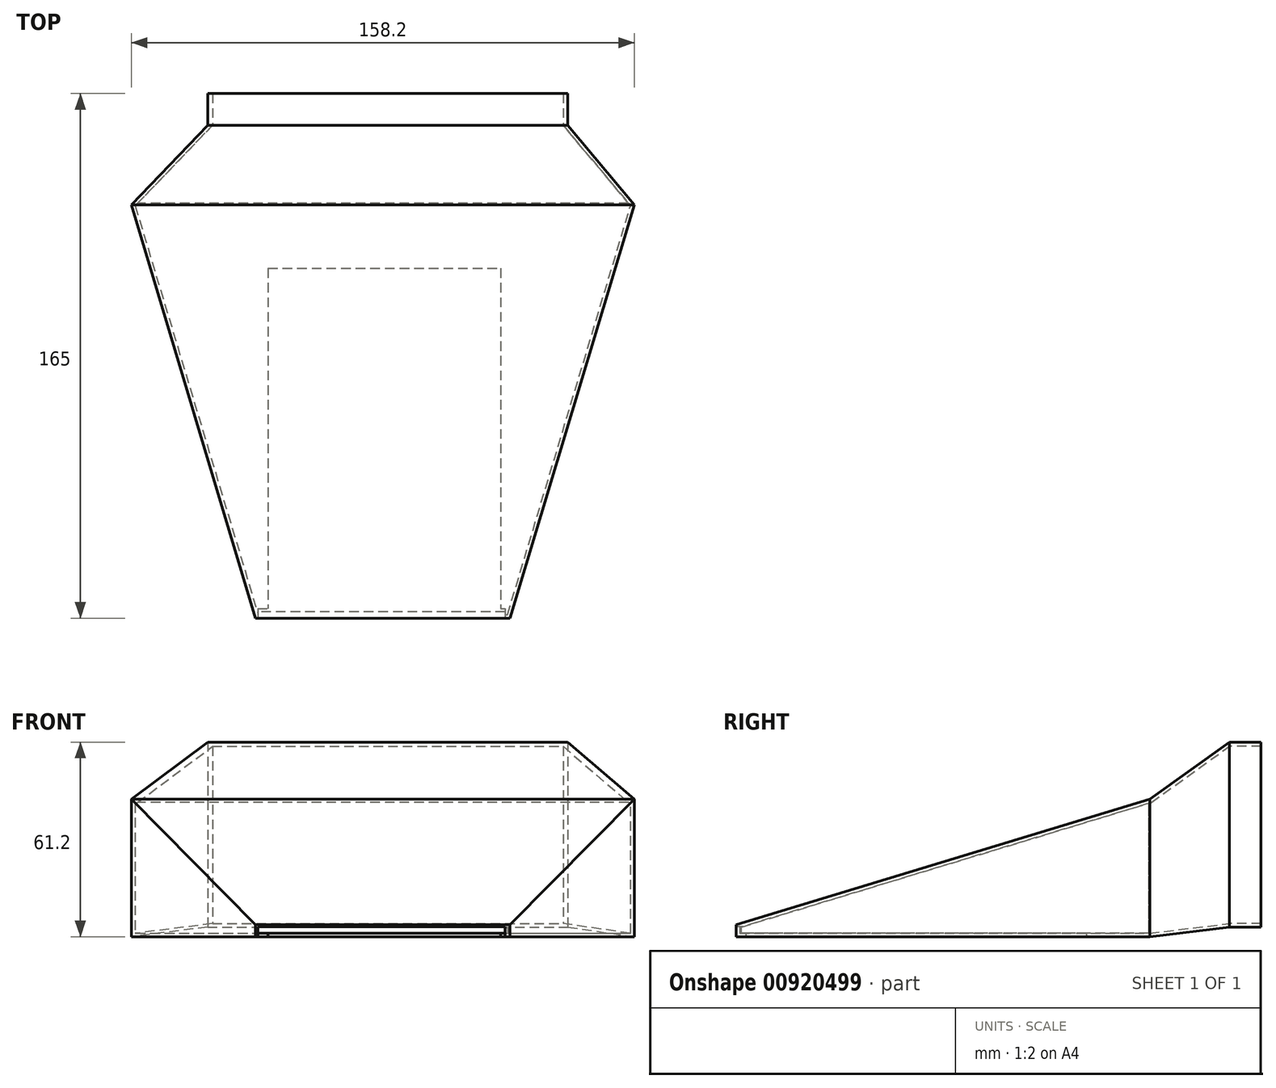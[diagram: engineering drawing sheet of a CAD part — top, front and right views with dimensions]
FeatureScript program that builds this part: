
annotation { "Feature Type Name" : "Feature", "Feature Type Description" : "" }
export const myFeature = defineFeature(function(context is Context, id is Id, definition is map)
    precondition{}
    {
        {
            var Q0;
            Q0=qCreatedBy(makeId("Front.planeOp"),FACE);
            var sketch = newSketch(context, id + "F0", { "sketchPlane" : qUnion([Q0])});
            skLineSegment(sketch, "E0.bottom", {"start": v(-55.06, 61.2) * mm, "end": v(58.14, 61.2) * mm});
            skLineSegment(sketch, "E0.top", {"start": v(-55.06, 3) * mm, "end": v(58.14, 3) * mm});
            skLineSegment(sketch, "E0.left", {"start": v(-55.06, 61.2) * mm, "end": v(-55.06, 3) * mm});
            skLineSegment(sketch, "E0.right", {"start": v(58.14, 61.2) * mm, "end": v(58.14, 3) * mm});
            skSolve(sketch);
        }
        {
            var Q0;
            Q0=qCreatedBy(makeId("Front.planeOp"),FACE);
            cPlane(context, id + "F1", {"entities" : qUnion([Q0]), "cplaneType" : CPlaneType.OFFSET, "offset" : 25 * mm, "width" : 150 * mm, "height" : 150 * mm});
        }
        {
            var Q0;
            Q0=qCreatedBy(id+"F1.planeOp",FACE);
            var sketch = newSketch(context, id + "F2", { "sketchPlane" : qUnion([Q0])});
            skLineSegment(sketch, "E1.bottom", {"start": v(-79.1, 43.2) * mm, "end": v(79.1, 43.2) * mm});
            skLineSegment(sketch, "E1.top", {"start": v(-79.1, 0) * mm, "end": v(79.1, 0) * mm});
            skLineSegment(sketch, "E1.left", {"start": v(-79.1, 43.2) * mm, "end": v(-79.1, 0) * mm});
            skLineSegment(sketch, "E1.right", {"start": v(79.1, 43.2) * mm, "end": v(79.1, 0) * mm});
            skSolve(sketch);
        }
        {
            var Q0;
            Q0=qCreatedBy(id+"F1.planeOp",FACE);
            cPlane(context, id + "F3", {"entities" : qUnion([Q0]), "cplaneType" : CPlaneType.OFFSET, "offset" : 130 * mm, "width" : 150 * mm, "height" : 150 * mm});
        }
        {
            var Q0;
            Q0=qCreatedBy(id+"F3.planeOp",FACE);
            var sketch = newSketch(context, id + "F4", { "sketchPlane" : qUnion([Q0])});
            skLineSegment(sketch, "E2.bottom", {"start": v(-40, 3.7) * mm, "end": v(40, 3.7) * mm});
            skLineSegment(sketch, "E2.top", {"start": v(-40, 0) * mm, "end": v(40, 0) * mm});
            skLineSegment(sketch, "E2.left", {"start": v(-40, 3.7) * mm, "end": v(-40, 0) * mm});
            skLineSegment(sketch, "E2.right", {"start": v(40, 3.7) * mm, "end": v(40, 0) * mm});
            skSolve(sketch);
        }
        {
            var Q0;
            Q0=makeQuery(id+"F0.imprint","IMPRINT",FACE,{"disambiguationData":[TD([[makeQuery(id+"F0.imprint","IMPRINT",EDGE,{"derivedFrom":sQuery(id+"F0.wireOp",EDGE,"E0.bottom")}),-1.0]])]});
            var Q1;
            Q1=makeQuery(id+"F2.imprint","IMPRINT",FACE,{"disambiguationData":[TD([[makeQuery(id+"F2.imprint","IMPRINT",EDGE,{"derivedFrom":sQuery(id+"F2.wireOp",EDGE,"E1.bottom")}),-1.0]])]});
            loft(context, id + "F5", {"sheetProfilesArray" : [{ "sheetProfileEntities" : qUnion([Q0]) }, { "sheetProfileEntities" : qUnion([Q1]) }]});
        }
        {
            var Q1;
            Q1=makeQuery(id+"F5.opLoft","CAP_FACE",FACE,{"disambiguationData":[OSD([makeQuery(id+"F2.imprint","IMPRINT",FACE,{"disambiguationData":[TD([[makeQuery(id+"F2.imprint","IMPRINT",EDGE,{"derivedFrom":sQuery(id+"F2.wireOp",EDGE,"E1.bottom")}),-1.0]])]})])],"isStart":true});
            var Q2;
            Q2=makeQuery(id+"F4.imprint","IMPRINT",FACE,{"disambiguationData":[TD([[makeQuery(id+"F4.imprint","IMPRINT",EDGE,{"derivedFrom":sQuery(id+"F4.wireOp",EDGE,"E2.bottom")}),-1.0]])]});
            loft(context, id + "F6", {"operationType" : NewBodyOperationType.ADD, "sheetProfilesArray" : [{ "sheetProfileEntities" : qUnion([Q1]) }, { "sheetProfileEntities" : qUnion([Q2]) }]});
        }
        {
            var Q0;
            Q0=makeQuery(id+"F6.opLoft","SWEPT_FACE",FACE,{"disambiguationData":[OSD([sQuery(id+"F2.wireOp",EDGE,"E1.top"),sQuery(id+"F2.wireOp",EDGE,"E1.left"),sQuery(id+"F2.wireOp",EDGE,"E1.right"),sQuery(id+"F4.wireOp",EDGE,"nRmw2GkL-DP8O-Oj1J-hX4m-Jp1XUWMUuBqS.bottom"),sQuery(id+"F4.wireOp",EDGE,"nRmw2GkL-DP8O-Oj1J-hX4m-Jp1XUWMUuBqS.left"),sQuery(id+"F4.wireOp",EDGE,"nRmw2GkL-DP8O-Oj1J-hX4m-Jp1XUWMUuBqS.right")])]});
            var sketch = newSketch(context, id + "F7", { "sketchPlane" : qUnion([Q0])});
            skLineSegment(sketch, "E3.bottom", {"start": v(-36.13, 44.96) * mm, "end": v(37.07, 44.96) * mm});
            skLineSegment(sketch, "E3.top", {"start": v(-36.13, 154.96) * mm, "end": v(37.07, 154.96) * mm});
            skLineSegment(sketch, "E3.left", {"start": v(-36.13, 44.96) * mm, "end": v(-36.13, 154.96) * mm});
            skLineSegment(sketch, "E3.right", {"start": v(37.07, 44.96) * mm, "end": v(37.07, 154.96) * mm});
            skSolve(sketch);
        }
        {
            var Q0;
            Q0=qSketchRegion(id+"F7",true);
            extrude(context, id + "F8", {"entities" : qUnion([Q0]), "operationType" : NewBodyOperationType.REMOVE, "oppositeDirection" : true, "depth" : 1.1 * mm, "offsetDistance" : 25 * mm});
        }
        {
            var Q0;
            Q0=makeQuery(id+"F5.opLoft","CAP_FACE",FACE,{"disambiguationData":[OSD([makeQuery(id+"F0.imprint","IMPRINT",FACE,{"disambiguationData":[TD([[makeQuery(id+"F0.imprint","IMPRINT",EDGE,{"derivedFrom":sQuery(id+"F0.wireOp",EDGE,"E0.bottom")}),-1.0]])]})])],"isStart":true});
            var Q1;
            Q1=makeQuery(id+"F8.boolean.opBoolean","COPY",FACE,{"derivedFrom":makeQuery(id+"F8.opExtrude","CAP_FACE",FACE,{"disambiguationData":[OSD([sQuery(id+"F7.wireOp",EDGE,"E3.bottom"),sQuery(id+"F7.wireOp",EDGE,"E3.top"),sQuery(id+"F7.wireOp",EDGE,"E3.left"),sQuery(id+"F7.wireOp",EDGE,"E3.right")])],"isStart":false})});
            shell(context, id + "F9", {"entities" : qUnion([Q0, Q1]), "thickness" : 1.1 * mm});
        }
        {
            var Q0;
            Q0=makeQuery(id+"F5.opLoft","CAP_FACE",FACE,{"disambiguationData":[OSD([makeQuery(id+"F0.imprint","IMPRINT",FACE,{"disambiguationData":[TD([[makeQuery(id+"F0.imprint","IMPRINT",EDGE,{"derivedFrom":sQuery(id+"F0.wireOp",EDGE,"E0.bottom")}),-1.0]])]})])],"isStart":true});
            extrude(context, id + "F10", {"entities" : qUnion([Q0]), "operationType" : NewBodyOperationType.ADD, "depth" : 10 * mm, "offsetDistance" : 25 * mm});
        }
        {
            var Q0;
            Q0=makeQuery(id+"F6.opLoft","CAP_FACE",FACE,{"disambiguationData":[OSD([makeQuery(id+"F4.imprint","IMPRINT",FACE,{"disambiguationData":[TD([[makeQuery(id+"F4.imprint","IMPRINT",EDGE,{"derivedFrom":sQuery(id+"F4.wireOp",EDGE,"E2.bottom")}),-1.0]])]})])],"isStart":true});
            var sketch = newSketch(context, id + "F11", { "sketchPlane" : qUnion([Q0])});
            skLineSegment(sketch, "E4.bottom", {"start": v(-39.34, 0) * mm, "end": v(38.4, 0) * mm});
            skLineSegment(sketch, "E4.top", {"start": v(-39.34, 3.15) * mm, "end": v(38.4, 3.15) * mm});
            skLineSegment(sketch, "E4.left", {"start": v(-39.34, 0) * mm, "end": v(-39.34, 3.15) * mm});
            skLineSegment(sketch, "E4.right", {"start": v(38.4, 0) * mm, "end": v(38.4, 3.15) * mm});
            skSolve(sketch);
        }
        {
            var Q0;
            Q0=qSketchRegion(id+"F11",true);
            extrude(context, id + "F12", {"entities" : qUnion([Q0]), "operationType" : NewBodyOperationType.REMOVE, "oppositeDirection" : true, "depth" : 3 * mm, "offsetDistance" : 25 * mm});
        }
    });
